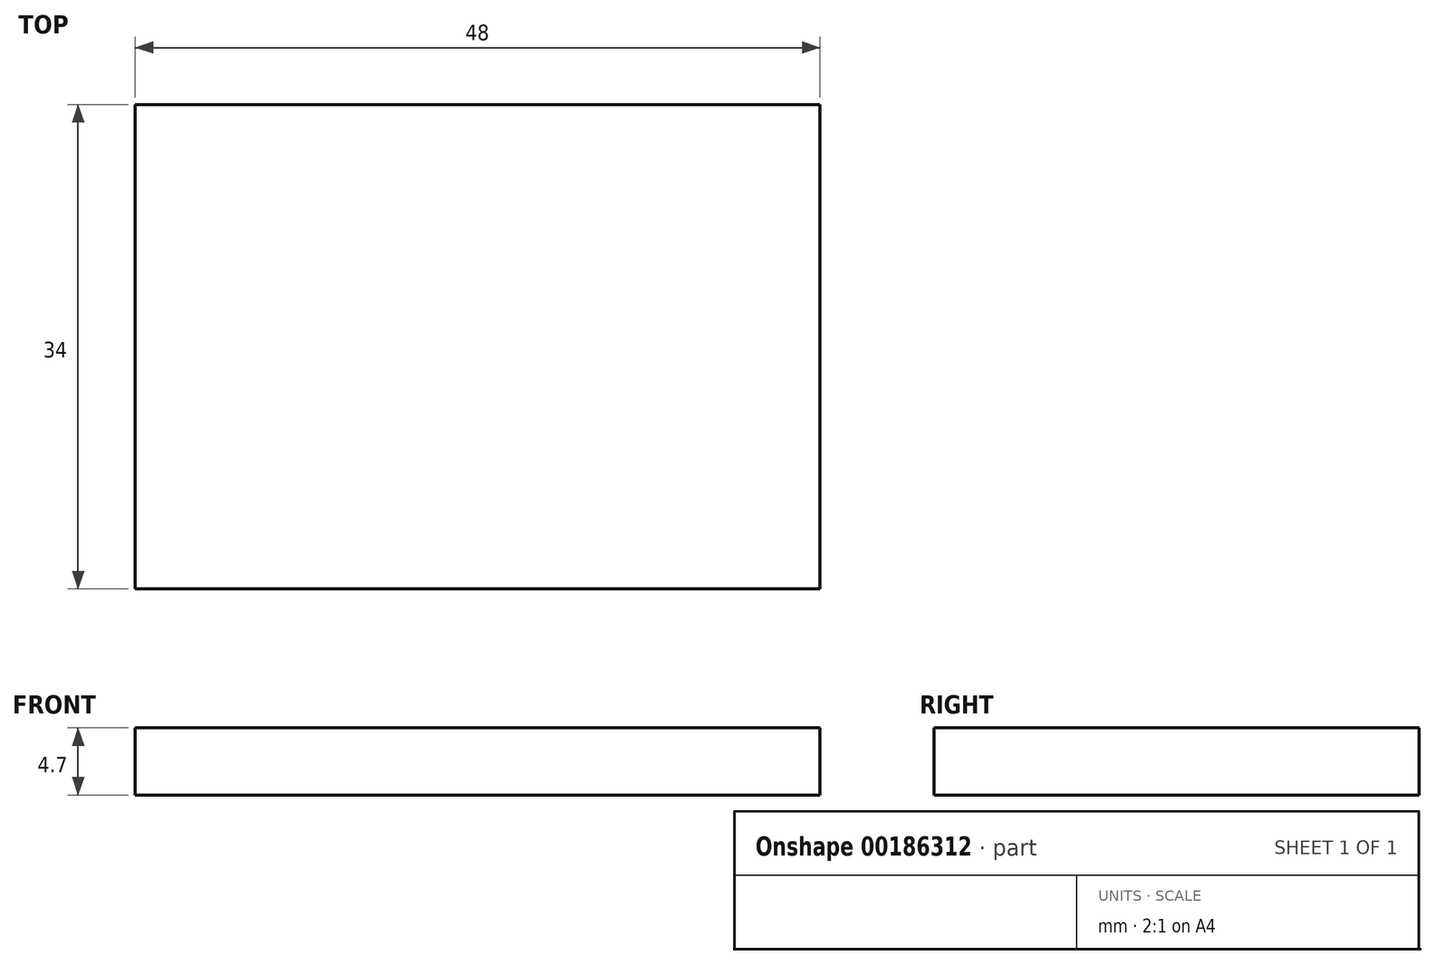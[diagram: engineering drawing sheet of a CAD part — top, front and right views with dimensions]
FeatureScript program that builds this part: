
annotation { "Feature Type Name" : "Feature", "Feature Type Description" : "" }
export const myFeature = defineFeature(function(context is Context, id is Id, definition is map)
    precondition{}
    {
        {
            var Q0;
            Q0=qCreatedBy(makeId("Top.planeOp"),FACE);
            var sketch = newSketch(context, id + "F0", { "sketchPlane" : qUnion([Q0])});
            skLineSegment(sketch, "E0.bottom", {"start": v(0, 0) * mm, "end": v(-48, 0) * mm});
            skLineSegment(sketch, "E0.top", {"start": v(0, 34) * mm, "end": v(-48, 34) * mm});
            skLineSegment(sketch, "E0.left", {"start": v(0, 0) * mm, "end": v(0, 34) * mm});
            skLineSegment(sketch, "E0.right", {"start": v(-48, 0) * mm, "end": v(-48, 34) * mm});
            skSolve(sketch);
        }
        {
            var Q0;
            Q0 = qSketchRegion(id + "F0", true);
            extrude(context, id + "F1", {"entities" : qUnion([Q0]), "depth" : 4.7 * mm});
        }
    });
